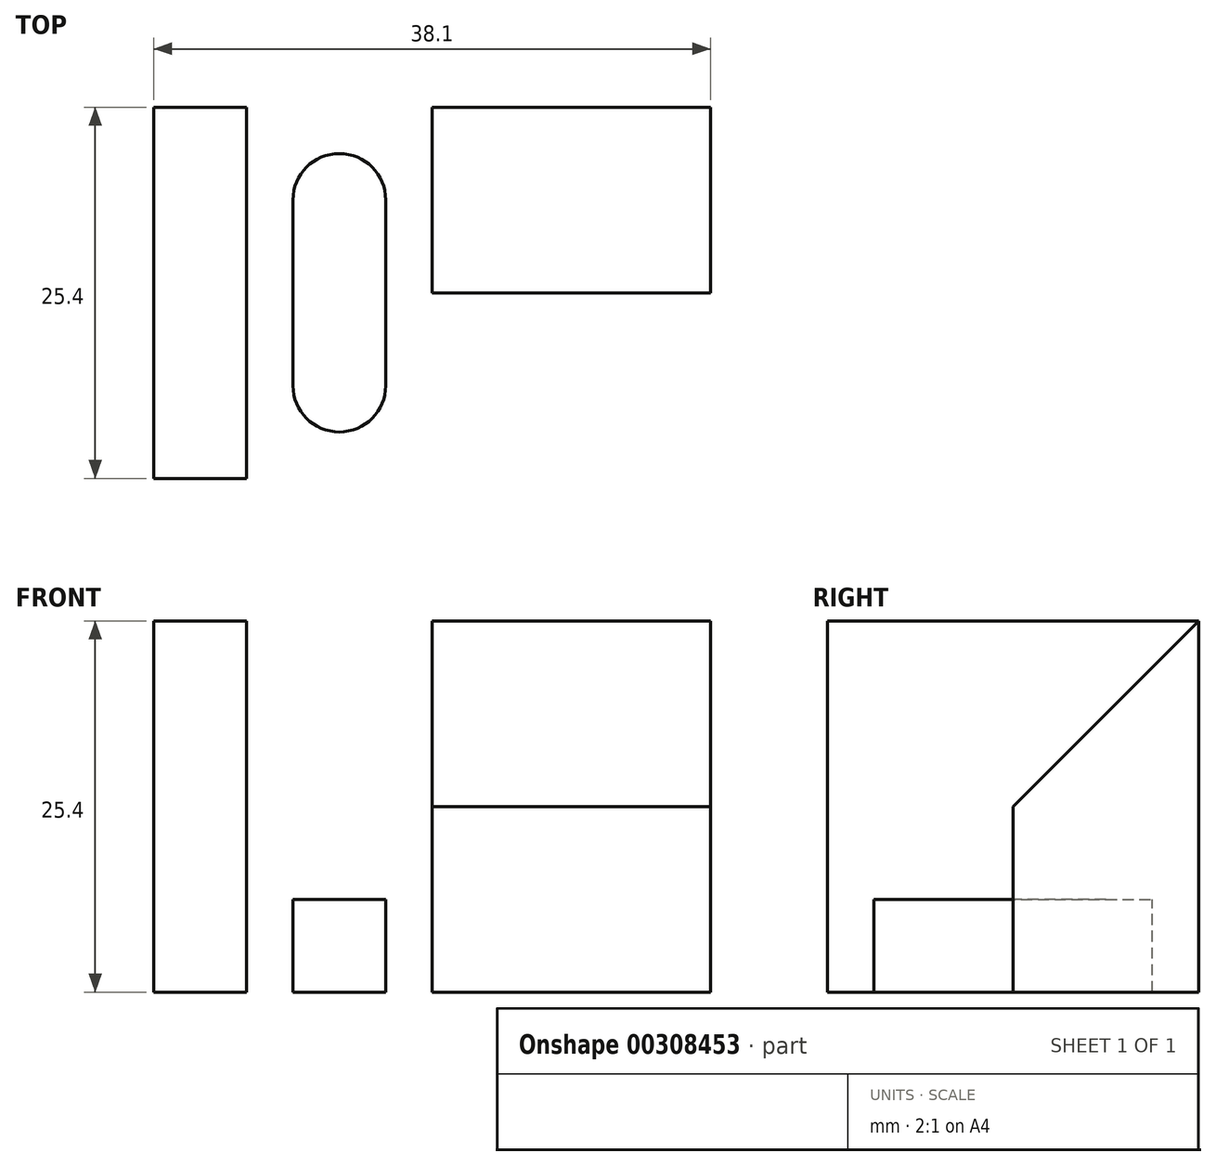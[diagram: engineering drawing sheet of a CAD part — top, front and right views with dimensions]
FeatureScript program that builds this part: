
annotation { "Feature Type Name" : "Feature", "Feature Type Description" : "" }
export const myFeature = defineFeature(function(context is Context, id is Id, definition is map)
    precondition{}
    {
        {
            var Q0;
            Q0=qCreatedBy(makeId("Front.planeOp"),FACE);
            var sketch = newSketch(context, id + "F0", { "sketchPlane" : qUnion([Q0])});
            skLineSegment(sketch, "E0", {"start": v(0, 0) * mm, "end": v(0, 25.4) * mm});
            skLineSegment(sketch, "E1", {"start": v(0, 25.4) * mm, "end": v(38.1, 25.4) * mm});
            skLineSegment(sketch, "E2", {"start": v(38.1, 25.4) * mm, "end": v(38.1, 0) * mm});
            skLineSegment(sketch, "E3", {"start": v(38.1, 0) * mm, "end": v(0, 0) * mm});
            skSolve(sketch);
        }
        {
            var Q0;
            Q0=makeQuery(id+"F0.imprint","IMPRINT",FACE,{"disambiguationData":[TD([[makeQuery(id+"F0.imprint","IMPRINT",EDGE,{"derivedFrom":sQuery(id+"F0.wireOp",EDGE,"E0")}),-1.0]])]});
            extrude(context, id + "F1", {"entities" : qUnion([Q0]), "oppositeDirection" : true, "depth" : 25.4 * mm});
        }
        {
            var Q0;
            Q0=makeQuery(id+"F1.opExtrude","SWEPT_FACE",FACE,{"disambiguationData":[OSD([sQuery(id+"F0.wireOp",EDGE,"E1")])]});
            var sketch = newSketch(context, id + "F2", { "sketchPlane" : qUnion([Q0])});
            skLineSegment(sketch, "E4", {"start": v(0, 25.4) * mm, "end": v(6.35, 25.4) * mm, "construction": true});
            skLineSegment(sketch, "E5", {"start": v(6.35, 25.4) * mm, "end": v(6.35, 0) * mm});
            skLineSegment(sketch, "E6", {"start": v(6.35, 0) * mm, "end": v(19.05, 0) * mm});
            skLineSegment(sketch, "E7", {"start": v(19.05, 0) * mm, "end": v(19.05, 25.4) * mm});
            skLineSegment(sketch, "E8", {"start": v(19.05, 25.4) * mm, "end": v(6.35, 25.4) * mm});
            skSolve(sketch);
        }
        {
            var Q0;
            Q0=makeQuery(id+"F2.imprint","IMPRINT",FACE,{"disambiguationData":[TD([[makeQuery(id+"F2.imprint","IMPRINT",EDGE,{"derivedFrom":sQuery(id+"F2.wireOp",EDGE,"E5")}),1.0]])]});
            extrude(context, id + "F3", {"entities" : qUnion([Q0]), "operationType" : NewBodyOperationType.REMOVE, "oppositeDirection" : true, "depth" : 19.05 * mm});
        }
        {
            var Q0;
            Q0=makeQuery(id+"F3.boolean.opBoolean","COPY",FACE,{"derivedFrom":makeQuery(id+"F3.opExtrude","CAP_FACE",FACE,{"disambiguationData":[OSD([sQuery(id+"F2.wireOp",EDGE,"E5"),sQuery(id+"F2.wireOp",EDGE,"E6"),sQuery(id+"F2.wireOp",EDGE,"E7"),sQuery(id+"F2.wireOp",EDGE,"E8")])],"isStart":false})});
            var sketch = newSketch(context, id + "F4", { "sketchPlane" : qUnion([Q0])});
            skLineSegment(sketch, "E9", {"start": v(12.7, 25.4) * mm, "end": v(12.7, 19.05) * mm});
            skLineSegment(sketch, "E10", {"start": v(12.7, 0) * mm, "end": v(12.7, 6.35) * mm, "construction": true});
            skArc(sketch, "E11", {"start": v(15.88, 19.05) * mm, "mid": v(12.7, 22.23) * mm, "end": v(9.53, 19.05) * mm});
            skArc(sketch, "E12", {"start": v(15.88, 6.35) * mm, "mid": v(12.7, 3.18) * mm, "end": v(9.53, 6.35) * mm});
            skLineSegment(sketch, "E13", {"start": v(15.88, 19.05) * mm, "end": v(15.88, 6.35) * mm});
            skLineSegment(sketch, "E14", {"start": v(9.53, 6.35) * mm, "end": v(9.53, 19.05) * mm});
            skSolve(sketch);
        }
        {
            var Q0;
            Q0=makeQuery(id+"F4.imprint","IMPRINT",FACE,{"disambiguationData":[TD([[makeQuery(id+"F4.imprint","IMPRINT",EDGE,{"derivedFrom":sQuery(id+"F4.wireOp",EDGE,"E12")}),-1.0]])]});
            extrude(context, id + "F5", {"entities" : qUnion([Q0]), "operationType" : NewBodyOperationType.REMOVE, "oppositeDirection" : true, "depth" : 25.4 * mm});
        }
        {
            var Q0;
            Q0=makeQuery(id+"F1.opExtrude","SWEPT_FACE",FACE,{"disambiguationData":[OSD([sQuery(id+"F0.wireOp",EDGE,"E2")])]});
            var sketch = newSketch(context, id + "F6", { "sketchPlane" : qUnion([Q0])});
            skLineSegment(sketch, "E15", {"start": v(0, 0) * mm, "end": v(0, 25.4) * mm});
            skLineSegment(sketch, "E16", {"start": v(0, 25.4) * mm, "end": v(25.4, 25.4) * mm});
            skLineSegment(sketch, "E17", {"start": v(0, 0) * mm, "end": v(12.7, 0) * mm});
            skLineSegment(sketch, "E18", {"start": v(12.7, 0) * mm, "end": v(12.7, 12.7) * mm});
            skLineSegment(sketch, "E19", {"start": v(12.7, 12.7) * mm, "end": v(25.4, 25.4) * mm});
            skSolve(sketch);
        }
        {
            var Q0;
            Q0=makeQuery(id+"F6.imprint","IMPRINT",FACE,{"disambiguationData":[TD([[makeQuery(id+"F6.imprint","IMPRINT",EDGE,{"derivedFrom":sQuery(id+"F6.wireOp",EDGE,"E15")}),1.0]])]});
            extrude(context, id + "F7", {"entities" : qUnion([Q0]), "operationType" : NewBodyOperationType.REMOVE, "oppositeDirection" : true, "depth" : 19.05 * mm});
        }
    });
